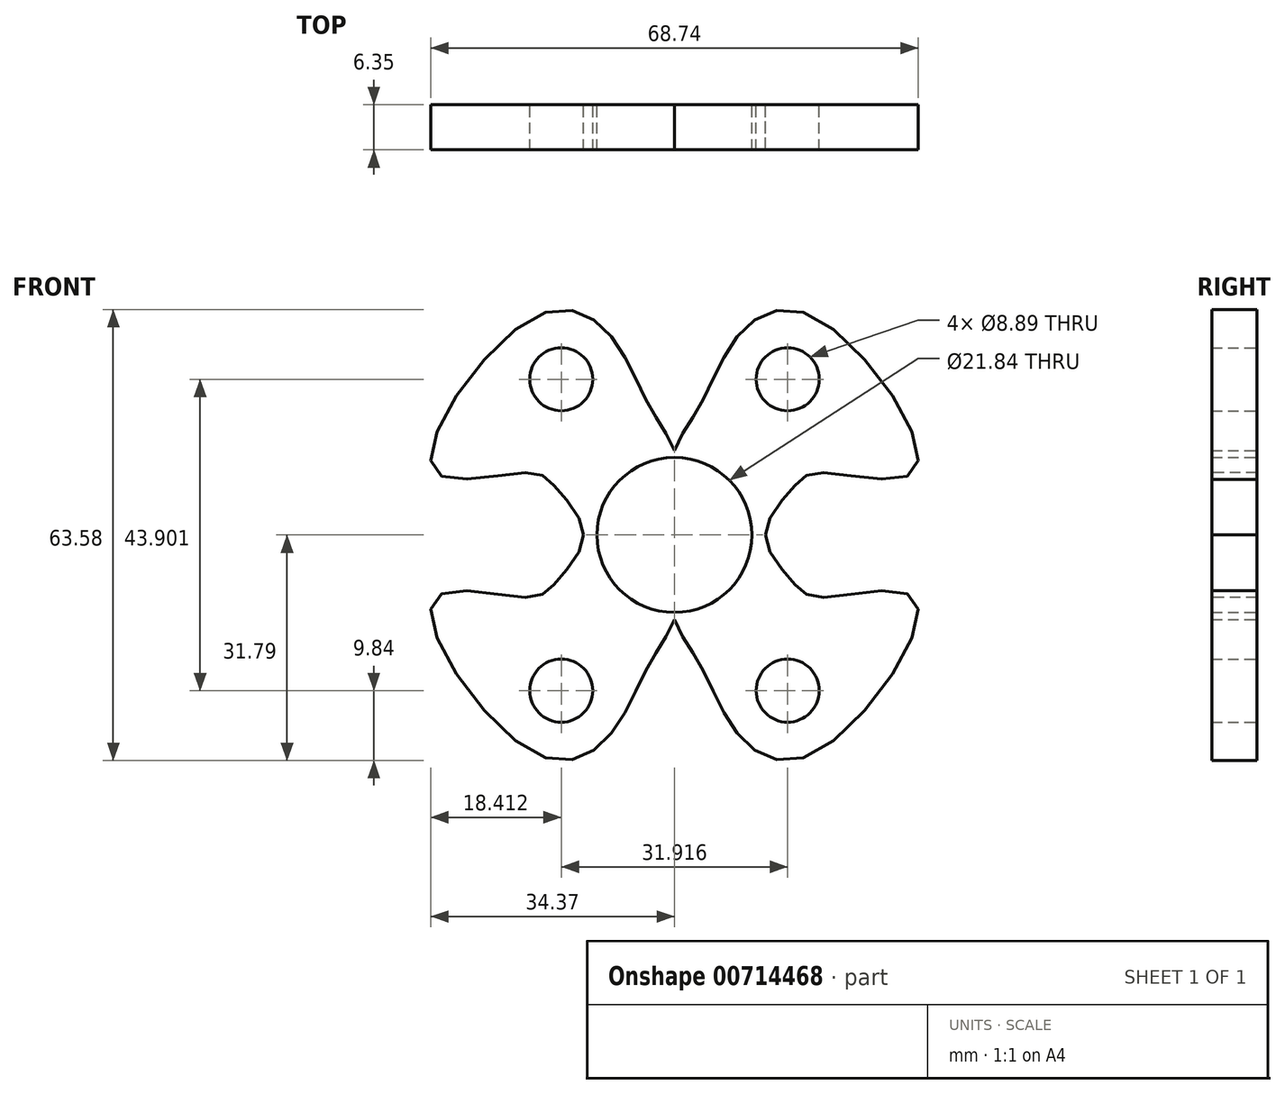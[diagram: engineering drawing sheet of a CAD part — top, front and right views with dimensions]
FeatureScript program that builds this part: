
annotation { "Feature Type Name" : "Feature", "Feature Type Description" : "" }
export const myFeature = defineFeature(function(context is Context, id is Id, definition is map)
    precondition{}
    {
        {
            var Q0;
            Q0=qCreatedBy(makeId("Front.planeOp"),FACE);
            var sketch = newSketch(context, id + "F0", { "sketchPlane" : qUnion([Q0])});
            skCircle(sketch, "E0", {"center": v(0, 0) * mm, "radius": 10.92 * mm});
            skFitSpline(sketch, "E1", {"points": [v(0, 11.9) * mm, v(3.7, 18.43) * mm, v(8.95, 28.04) * mm, v(19.6, 30.8) * mm, v(34, 9.23) * mm, v(20.77, 8.8) * mm, v(16.56, 6.52) * mm, v(12.8, 0) * mm], "startDerivative": vector(21.82, 59.7) * mm, "endDerivative": vector(4.48, -49.75) * mm});
            skFitSpline(sketch, "E2.MirrorCS", {"points": [v(0, -11.9) * mm, v(3.7, -18.43) * mm, v(8.95, -28.04) * mm, v(19.6, -30.8) * mm, v(34, -9.23) * mm, v(20.77, -8.8) * mm, v(16.56, -6.52) * mm, v(12.8, 0) * mm], "startDerivative": vector(21.82, -59.7) * mm, "endDerivative": vector(4.48, 49.75) * mm});
            skFitSpline(sketch, "E3.MirrorCS", {"points": [v(0, 11.9) * mm, v(3.7, 18.43) * mm, v(8.95, 28.04) * mm, v(19.6, 30.8) * mm, v(34, 9.23) * mm, v(20.77, 8.8) * mm, v(16.56, 6.52) * mm, v(12.8, 0) * mm], "startDerivative": vector(21.82, 59.7) * mm, "endDerivative": vector(4.48, -49.75) * mm});
            skFitSpline(sketch, "E4.MirrorCS", {"points": [v(0, -11.9) * mm, v(-3.7, -18.43) * mm, v(-8.95, -28.04) * mm, v(-19.6, -30.8) * mm, v(-34, -9.23) * mm, v(-20.77, -8.8) * mm, v(-16.56, -6.52) * mm, v(-12.8, 0) * mm], "startDerivative": vector(-21.82, -59.7) * mm, "endDerivative": vector(-4.48, 49.75) * mm});
            skFitSpline(sketch, "E5.MirrorCS", {"points": [v(0, 11.9) * mm, v(-3.7, 18.43) * mm, v(-8.95, 28.04) * mm, v(-19.6, 30.8) * mm, v(-34, 9.23) * mm, v(-20.77, 8.8) * mm, v(-16.56, 6.52) * mm, v(-12.8, 0) * mm], "startDerivative": vector(-21.82, 59.7) * mm, "endDerivative": vector(-4.48, -49.75) * mm});
            skCircle(sketch, "E6", {"center": v(-15.96, 21.95) * mm, "radius": 4.44 * mm});
            skCircle(sketch, "E7.MirrorC", {"center": v(-15.96, -21.95) * mm, "radius": 4.44 * mm});
            skCircle(sketch, "E8.MirrorC", {"center": v(15.96, -21.95) * mm, "radius": 4.44 * mm});
            skCircle(sketch, "E9.MirrorC", {"center": v(15.96, 21.95) * mm, "radius": 4.44 * mm});
            skSolve(sketch);
        }
        {
            var Q0;
            Q0=makeQuery(id+"F0.imprint","IMPRINT",FACE,{"disambiguationData":[TD([[makeQuery(id+"F0.imprint","IMPRINT",EDGE,{"derivedFrom":sQuery(id+"F0.wireOp",EDGE,"E0")}),-1.0]])]});
            extrude(context, id + "F1", {"entities" : qUnion([Q0]), "depth" : 6.35 * mm, "offsetDistance" : 25.4 * mm});
        }
        {
            var Q0;
            Q0=makeQuery(id+"F0.imprint","IMPRINT",FACE,{"disambiguationData":[TD([[makeQuery(id+"F0.imprint","IMPRINT",EDGE,{"derivedFrom":sQuery(id+"F0.wireOp",EDGE,"E0")}),1.0]])]});
            extrude(context, id + "F2", {"entities" : qUnion([Q0]), "depth" : 2.54 * mm, "offsetDistance" : 25.4 * mm, "hasSecondDirection" : true, "secondDirectionOppositeDirection" : true, "secondDirectionDepth" : 0 * mm});
        }
        {
            var Q0;
            Q0=makeQuery(id+"F2.opExtrude","SWEPT_BODY",BODY,{"disambiguationData":[OSD([sQuery(id+"F0.wireOp",EDGE,"E0")])]});
            deleteBodies(context, id + "F3", {"entities" : qUnion([Q0])});
        }
    });
